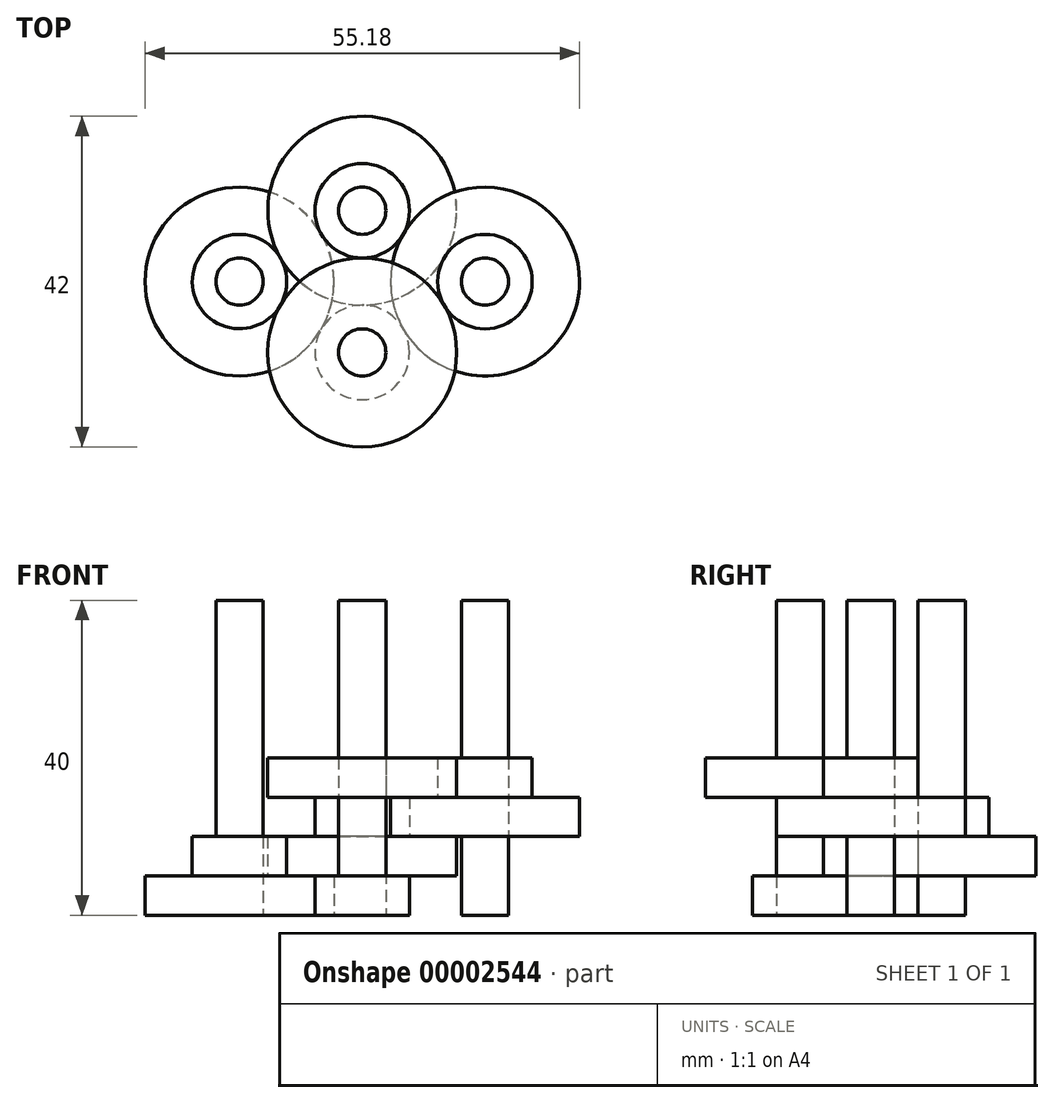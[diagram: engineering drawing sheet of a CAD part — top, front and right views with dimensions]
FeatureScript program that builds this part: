
annotation { "Feature Type Name" : "Feature", "Feature Type Description" : "" }
export const myFeature = defineFeature(function(context is Context, id is Id, definition is map)
    precondition{}
    {
        {
            var Q0;
            Q0=qCreatedBy(makeId("Top.planeOp"),FACE);
            var sketch = newSketch(context, id + "F0", { "sketchPlane" : qUnion([Q0])});
            skCircle(sketch, "E0", {"center": v(0, 0) * mm, "radius": 3 * mm});
            skCircle(sketch, "E1", {"center": v(-15.59, 9) * mm, "radius": 3 * mm});
            skCircle(sketch, "E2", {"center": v(0, 18) * mm, "radius": 3 * mm});
            skCircle(sketch, "E3", {"center": v(15.59, 9) * mm, "radius": 3 * mm});
            skLineSegment(sketch, "E4", {"start": v(-15.59, 9) * mm, "end": v(0, 0) * mm, "construction": true});
            skLineSegment(sketch, "E5", {"start": v(15.59, 9) * mm, "end": v(0, 0) * mm, "construction": true});
            skLineSegment(sketch, "E6", {"start": v(0, 18) * mm, "end": v(0, 0) * mm, "construction": true});
            skLineSegment(sketch, "E7", {"start": v(-15.59, 9) * mm, "end": v(0, 18) * mm, "construction": true});
            skLineSegment(sketch, "E8", {"start": v(15.59, 9) * mm, "end": v(0, 18) * mm, "construction": true});
            skCircle(sketch, "E9", {"center": v(0, 0) * mm, "radius": 6 * mm, "construction": true});
            skCircle(sketch, "E10", {"center": v(-15.59, 9) * mm, "radius": 12 * mm, "construction": true});
            skCircle(sketch, "E11", {"center": v(-15.59, 9) * mm, "radius": 6 * mm, "construction": true});
            skCircle(sketch, "E12", {"center": v(0, 18) * mm, "radius": 12 * mm, "construction": true});
            skCircle(sketch, "E13", {"center": v(0, 18) * mm, "radius": 6 * mm, "construction": true});
            skCircle(sketch, "E14", {"center": v(15.59, 9) * mm, "radius": 6 * mm, "construction": true});
            skCircle(sketch, "E15", {"center": v(0, 0) * mm, "radius": 12 * mm, "construction": true});
            skCircle(sketch, "E16", {"center": v(0, 0) * mm, "radius": 30 * mm, "construction": true});
            skCircle(sketch, "E17", {"center": v(15.59, 9) * mm, "radius": 12 * mm, "construction": true});
            skLineSegment(sketch, "E18", {"start": v(-27.5, -12) * mm, "end": v(27.5, -12) * mm, "construction": true});
            skSolve(sketch);
        }
        {
            var Q0;
            Q0 = qSketchRegion(id + "F0", true);
            extrude(context, id + "F1", {"entities" : qUnion([Q0]), "depth" : 40 * mm});
        }
        {
            var Q0;
            Q0=qCreatedBy(makeId("Top.planeOp"),FACE);
            var sketch = newSketch(context, id + "F2", { "sketchPlane" : qUnion([Q0])});
            skCircle(sketch, "E19", {"center": v(0, 0) * mm, "radius": 6 * mm});
            skSolve(sketch);
        }
        {
            var Q0;
            Q0=makeQuery(id+"F2.imprint","IMPRINT",FACE,{"disambiguationData":[TD([[makeQuery(id+"F2.imprint","IMPRINT",EDGE,{"derivedFrom":sQuery(id+"F2.wireOp",EDGE,"E19")}),1.0]])]});
            extrude(context, id + "F3", {"entities" : qUnion([Q0]), "operationType" : NewBodyOperationType.ADD, "depth" : 5 * mm});
        }
        {
            var Q0;
            Q0=qCreatedBy(makeId("Top.planeOp"),FACE);
            cPlane(context, id + "F4", {"entities" : qUnion([Q0]), "cplaneType" : CPlaneType.OFFSET, "offset" : 5 * mm, "width" : 150 * mm, "height" : 150 * mm});
        }
        {
            var Q0;
            Q0=qCreatedBy(makeId("Top.planeOp"),FACE);
            var sketch = newSketch(context, id + "F5", { "sketchPlane" : qUnion([Q0])});
            skCircle(sketch, "E20", {"center": v(-15.59, 9) * mm, "radius": 12 * mm});
            skSolve(sketch);
        }
        {
            var Q0;
            Q0 = qSketchRegion(id + "F5", true);
            extrude(context, id + "F6", {"entities" : qUnion([Q0]), "depth" : 5 * mm});
        }
        {
            var Q0;
            Q0=makeQuery(id+"F6.opExtrude","CAP_FACE",FACE,{"disambiguationData":[OSD([sQuery(id+"F5.wireOp",EDGE,"E20")])],"isStart":false});
            var sketch = newSketch(context, id + "F7", { "sketchPlane" : qUnion([Q0])});
            skCircle(sketch, "E21", {"center": v(-15.59, 9) * mm, "radius": 6 * mm});
            skSolve(sketch);
        }
        {
            var Q0;
            Q0 = qSketchRegion(id + "F7", true);
            extrude(context, id + "F8", {"entities" : qUnion([Q0]), "depth" : 5 * mm});
        }
        {
            var Q0;
            Q0=qCreatedBy(id+"F4.planeOp",FACE);
            var sketch = newSketch(context, id + "F9", { "sketchPlane" : qUnion([Q0])});
            skCircle(sketch, "E22", {"center": v(0, 18) * mm, "radius": 12 * mm});
            skSolve(sketch);
        }
        {
            var Q0;
            Q0 = qSketchRegion(id + "F9", true);
            extrude(context, id + "F10", {"entities" : qUnion([Q0]), "depth" : 5 * mm});
        }
        {
            var Q0;
            Q0=makeQuery(id+"F10.opExtrude","CAP_FACE",FACE,{"disambiguationData":[OSD([sQuery(id+"F9.wireOp",EDGE,"E22")])],"isStart":false});
            var sketch = newSketch(context, id + "F11", { "sketchPlane" : qUnion([Q0])});
            skCircle(sketch, "E23", {"center": v(0, 18) * mm, "radius": 6 * mm});
            skSolve(sketch);
        }
        {
            var Q0;
            Q0=makeQuery(id+"F11.imprint","IMPRINT",FACE,{"disambiguationData":[TD([[makeQuery(id+"F11.imprint","IMPRINT",EDGE,{"derivedFrom":sQuery(id+"F11.wireOp",EDGE,"E23")}),1.0]])]});
            extrude(context, id + "F12", {"entities" : qUnion([Q0]), "depth" : 5 * mm});
        }
        {
            var Q0;
            Q0=makeQuery(id+"F10.opExtrude","CAP_FACE",FACE,{"disambiguationData":[OSD([sQuery(id+"F9.wireOp",EDGE,"E22")])],"isStart":false});
            var sketch = newSketch(context, id + "F13", { "sketchPlane" : qUnion([Q0])});
            skCircle(sketch, "E24", {"center": v(15.59, 9) * mm, "radius": 12 * mm});
            skSolve(sketch);
        }
        {
            var Q0;
            Q0 = qSketchRegion(id + "F13", true);
            extrude(context, id + "F14", {"entities" : qUnion([Q0]), "depth" : 5 * mm});
        }
        {
            var Q0;
            Q0=makeQuery(id+"F14.opExtrude","CAP_FACE",FACE,{"disambiguationData":[OSD([sQuery(id+"F13.wireOp",EDGE,"E24")])],"isStart":false});
            var sketch = newSketch(context, id + "F15", { "sketchPlane" : qUnion([Q0])});
            skCircle(sketch, "E25", {"center": v(15.59, 9) * mm, "radius": 6 * mm});
            skSolve(sketch);
        }
        {
            var Q0;
            Q0 = qSketchRegion(id + "F15", true);
            extrude(context, id + "F16", {"entities" : qUnion([Q0]), "depth" : 5 * mm});
        }
        {
            var Q0;
            Q0=makeQuery(id+"F14.opExtrude","CAP_FACE",FACE,{"disambiguationData":[OSD([sQuery(id+"F13.wireOp",EDGE,"E24")])],"isStart":false});
            var sketch = newSketch(context, id + "F17", { "sketchPlane" : qUnion([Q0])});
            skCircle(sketch, "E26", {"center": v(0, 0) * mm, "radius": 12 * mm});
            skSolve(sketch);
        }
        {
            var Q0;
            Q0 = qSketchRegion(id + "F17", true);
            extrude(context, id + "F18", {"entities" : qUnion([Q0]), "depth" : 5 * mm});
        }
    });
